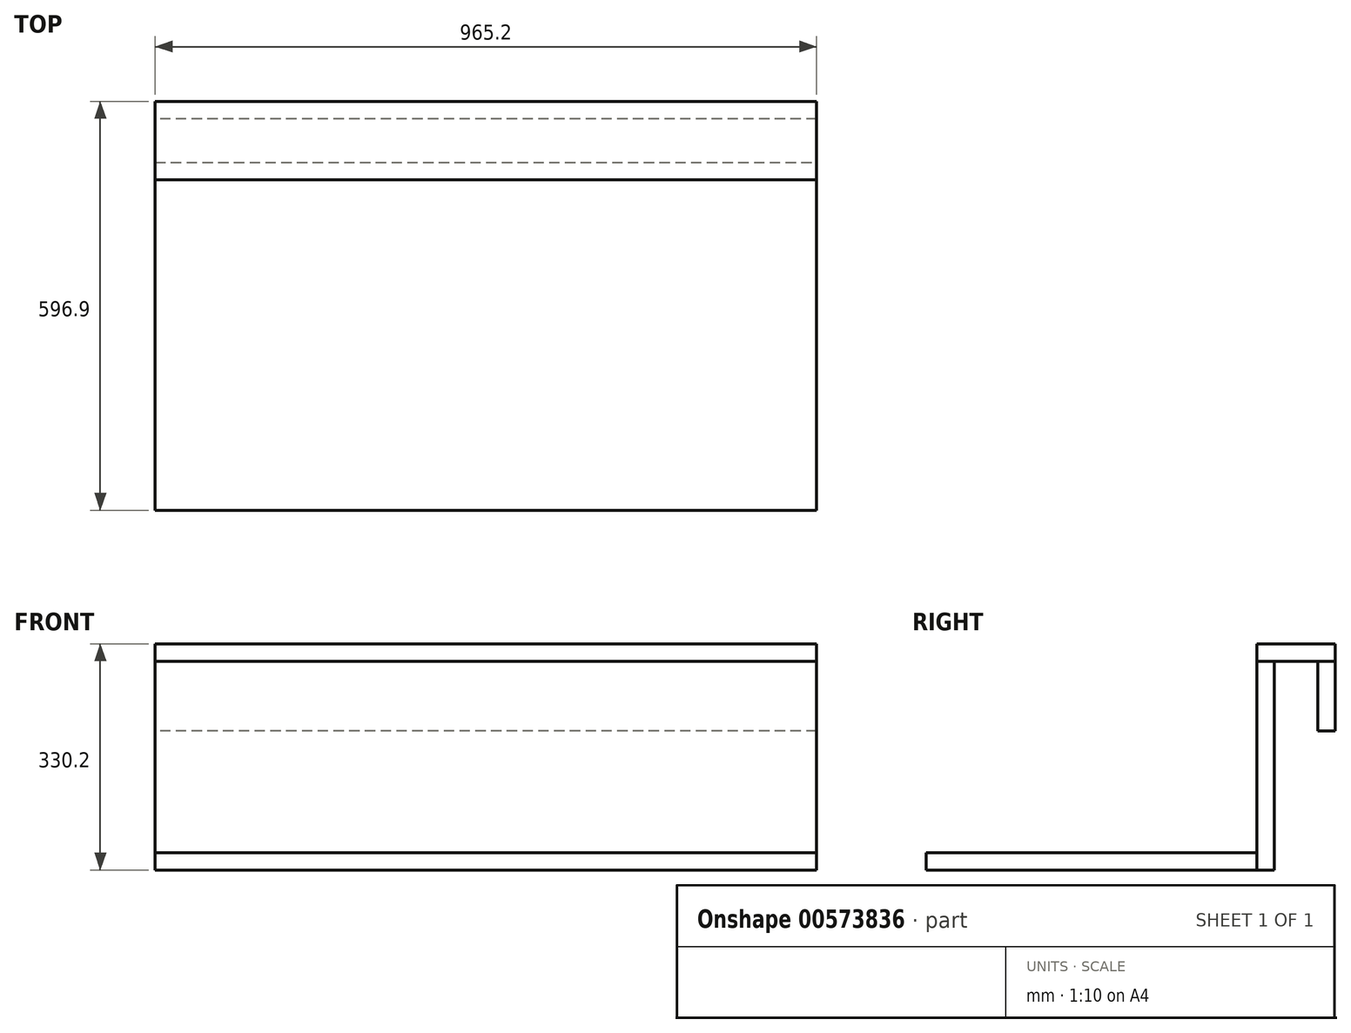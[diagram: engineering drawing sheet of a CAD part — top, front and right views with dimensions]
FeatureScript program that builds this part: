
annotation { "Feature Type Name" : "Feature", "Feature Type Description" : "" }
export const myFeature = defineFeature(function(context is Context, id is Id, definition is map)
    precondition{}
    {
        {
            var Q0;
            Q0=qCreatedBy(makeId("Front.planeOp"),FACE);
            var sketch = newSketch(context, id + "F0", { "sketchPlane" : qUnion([Q0])});
            skLineSegment(sketch, "E0.bottom", {"start": v(-482.6, 0) * mm, "end": v(482.6, 0) * mm});
            skLineSegment(sketch, "E0.top", {"start": v(-482.6, 304.8) * mm, "end": v(482.6, 304.8) * mm});
            skLineSegment(sketch, "E0.left", {"start": v(-482.6, 0) * mm, "end": v(-482.6, 304.8) * mm});
            skLineSegment(sketch, "E0.right", {"start": v(482.6, 0) * mm, "end": v(482.6, 304.8) * mm});
            skSolve(sketch);
        }
        {
            var Q0;
            Q0 = qSketchRegion(id + "F0", true);
            extrude(context, id + "F1", {"entities" : qUnion([Q0]), "depth" : 25.4 * mm, "offsetDistance" : 25.4 * mm});
        }
        {
            var Q0;
            Q0=makeQuery(id+"F1.opExtrude","CAP_FACE",FACE,{"disambiguationData":[OSD([sQuery(id+"F0.wireOp",EDGE,"E0.bottom"),sQuery(id+"F0.wireOp",EDGE,"E0.top"),sQuery(id+"F0.wireOp",EDGE,"E0.left"),sQuery(id+"F0.wireOp",EDGE,"E0.right")])],"isStart":false});
            var sketch = newSketch(context, id + "F2", { "sketchPlane" : qUnion([Q0])});
            skLineSegment(sketch, "E1.bottom", {"start": v(-482.6, 0) * mm, "end": v(482.6, 0) * mm});
            skLineSegment(sketch, "E1.top", {"start": v(-482.6, 25.4) * mm, "end": v(482.6, 25.4) * mm});
            skLineSegment(sketch, "E1.left", {"start": v(-482.6, 0) * mm, "end": v(-482.6, 25.4) * mm});
            skLineSegment(sketch, "E1.right", {"start": v(482.6, 0) * mm, "end": v(482.6, 25.4) * mm});
            skSolve(sketch);
        }
        {
            var Q0;
            Q0 = qSketchRegion(id + "F2", true);
            extrude(context, id + "F3", {"entities" : qUnion([Q0]), "depth" : 482.6 * mm, "offsetDistance" : 25.4 * mm});
        }
        {
            var Q0;
            Q0=makeQuery(id+"F1.opExtrude","SWEPT_FACE",FACE,{"disambiguationData":[OSD([sQuery(id+"F0.wireOp",EDGE,"E0.top")])]});
            var sketch = newSketch(context, id + "F4", { "sketchPlane" : qUnion([Q0])});
            skLineSegment(sketch, "E2.bottom", {"start": v(-482.6, -25.4) * mm, "end": v(482.6, -25.4) * mm});
            skLineSegment(sketch, "E2.top", {"start": v(-482.6, 88.9) * mm, "end": v(482.6, 88.9) * mm});
            skLineSegment(sketch, "E2.left", {"start": v(-482.6, -25.4) * mm, "end": v(-482.6, 88.9) * mm});
            skLineSegment(sketch, "E2.right", {"start": v(482.6, -25.4) * mm, "end": v(482.6, 88.9) * mm});
            skSolve(sketch);
        }
        {
            var Q0;
            Q0 = qSketchRegion(id + "F4", true);
            extrude(context, id + "F5", {"entities" : qUnion([Q0]), "depth" : 25.4 * mm, "offsetDistance" : 25.4 * mm});
        }
        {
            var Q0;
            Q0=makeQuery(id+"F5.opExtrude","CAP_FACE",FACE,{"disambiguationData":[OSD([sQuery(id+"F4.wireOp",EDGE,"E2.bottom"),sQuery(id+"F4.wireOp",EDGE,"E2.top"),sQuery(id+"F4.wireOp",EDGE,"E2.left"),sQuery(id+"F4.wireOp",EDGE,"E2.right")])],"isStart":true});
            var sketch = newSketch(context, id + "F6", { "sketchPlane" : qUnion([Q0])});
            skLineSegment(sketch, "E3.bottom", {"start": v(482.6, -88.9) * mm, "end": v(-482.6, -88.9) * mm});
            skLineSegment(sketch, "E3.top", {"start": v(482.6, -63.5) * mm, "end": v(-482.6, -63.5) * mm});
            skLineSegment(sketch, "E3.left", {"start": v(482.6, -88.9) * mm, "end": v(482.6, -63.5) * mm});
            skLineSegment(sketch, "E3.right", {"start": v(-482.6, -88.9) * mm, "end": v(-482.6, -63.5) * mm});
            skSolve(sketch);
        }
        {
            var Q0;
            Q0 = qSketchRegion(id + "F6", true);
            extrude(context, id + "F7", {"entities" : qUnion([Q0]), "depth" : 101.6 * mm, "offsetDistance" : 25.4 * mm});
        }
    });
